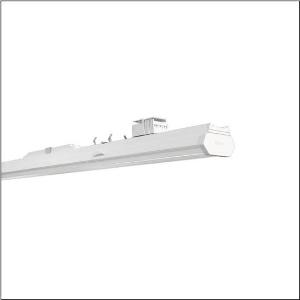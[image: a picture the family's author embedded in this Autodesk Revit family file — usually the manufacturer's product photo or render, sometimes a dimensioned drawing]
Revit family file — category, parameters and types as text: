
# Revit family: licross_r__11_protected_ho_51tp11cn4exs_0205
name_source: partatom
category: Lighting Fixtures
units: mm (PartAtom-declared; Revit-internal decimal feet)

## family parameters
Cut with Voids When Loaded = No
Host = Face
Light Source = No
Part Type = Normal
Room Calculation Point = No
Round Connector Dimension = Use Diameter
Shared = No

## types (1)
- --- (1 x LED, 14460 lm, 77.6 W, 4000K)
    Apparent Load = 78 VA
    CIE Flux Codes = 84 94 98 99 100
    Color Rendering = 80
    Color Temperature = 4000K
    Default Elevation = 1800 mm
    Description = Licross® 11 Protected HO, luminaire insert, of sheet steel, galvanised, coil coated, white, length: 1.500mm, width: 90mm, height: 101mm, LED rated luminous flux: 14.460lm, light colour: 840, control gear: ON/OFF Multilumen, CLOi, with plug, 3-pole, with phase selection, mains connection: 220..240V, AC, 50/60Hz, start of lifetime: 78W, end of service life: 87W, halogen-free wiring, primary light control with lens, of plastic, primary optical cover: cover, of PMMA, light emission: direct distribution, primary light characteristic: symmetric, protection rating (complete): IP64, insulation class (complete): insulation class I (protective earthing), certification: CE, ENEC, VDE, UKCA, protection symbol: D if used in an environment with conductive dust loads with corresponding accessories, impact resistance: IK06, permissible ambient temperature for indoor applications: -35..+35°C, corresponds to IFS (International Featured Standards) requirements for safety and quality in the food industry, reducing of maximum allowable ambient temperature of 5°C with ceiling mounting, LABS conformity tested according to VDMA 24364:2018-05, packaging unit: 1 piece
    Height = 92 mm
    Lamp = 1 x LED
    Lamp Light Flux = 14460 lm
    Lamp Power = 77.6 W
    Lamp count = 1
    Length = 1500 mm
    Luminous efficacy = 186 lm/W
    Manufacturer = Siteco
    ModVariant = No
    Model = 51TP11CN4EXS
    Mounting Place = Ceiling
    Mounting Type = Pendant
    Number of Poles = 1
    OnlyDefault = Yes
    Power Factor = 1
    Product Name = Licross® 11 Protected HO
    Product group = luminaire insert
    ProductGroupID = 901
    Protection Class = Protection class I
    Protection Degree = IP 64
    RLX_Detail_Level = 1
    RLX_Emergency_Light_Flux = 0 lm
    RLX_Emergency_Type = 0
    RLX_Emergency_Type_DB = No
    RlxData = <blob elided: 22077 chars, md5=e943c960>
    Socket = socket
    Standby Power = 0 W
    System Light Flux = 14460 lm
    System Power = 78 W
    Type Comments = factory setting: luminous flux: 100 % | (A | C | E) | 181 mA
    Type Image = l_1256148.jpg
    URL = http://relux.com
    VarID = @adj_019331
    Voltage = 0 V
    Weight = 0.00 kg
    Width = 88 mm

## geometry (parser evidence)
native form markers: Blend x4, Sweep x12
no freeform markers — native parametric forms only
